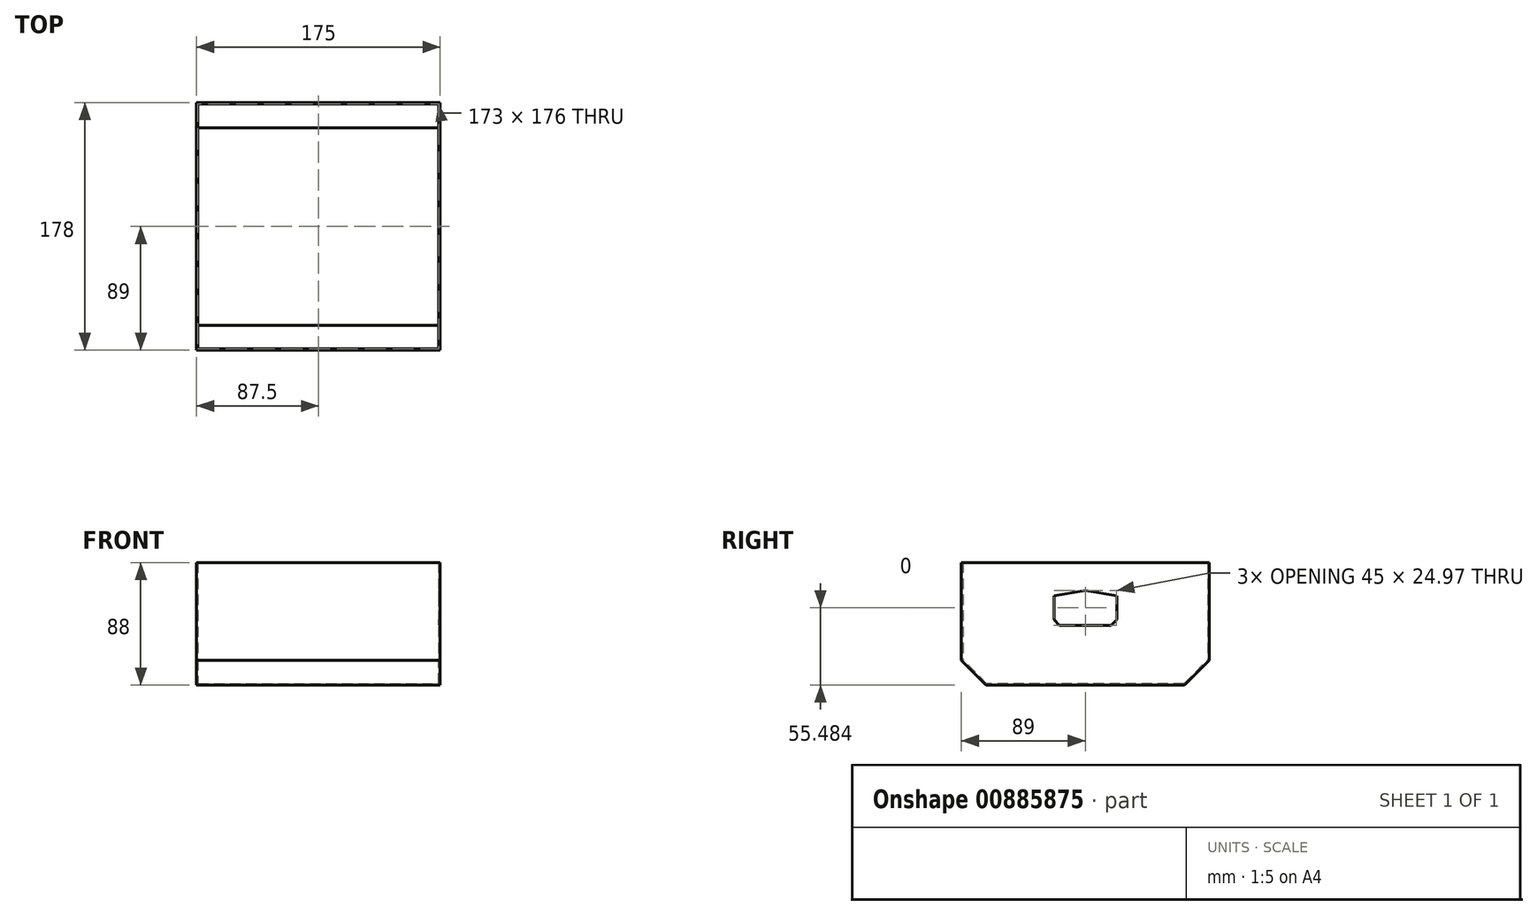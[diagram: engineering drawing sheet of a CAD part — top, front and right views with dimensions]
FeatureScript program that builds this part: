
annotation { "Feature Type Name" : "Feature", "Feature Type Description" : "" }
export const myFeature = defineFeature(function(context is Context, id is Id, definition is map)
    precondition{}
    {
        {
            var Q0;
            Q0=qCreatedBy(makeId("Top.planeOp"),FACE);
            var sketch = newSketch(context, id + "F0", { "sketchPlane" : qUnion([Q0])});
            skLineSegment(sketch, "E0.bottom", {"start": v(0, 0) * mm, "end": v(175, 0) * mm});
            skLineSegment(sketch, "E0.top", {"start": v(0, -178) * mm, "end": v(175, -178) * mm});
            skLineSegment(sketch, "E0.left", {"start": v(0, 0) * mm, "end": v(0, -178) * mm});
            skLineSegment(sketch, "E0.right", {"start": v(175, 0) * mm, "end": v(175, -178) * mm});
            skSolve(sketch);
        }
        {
            var Q0;
            Q0 = qSketchRegion(id + "F0", true);
            extrude(context, id + "F1", {"entities" : qUnion([Q0]), "depth" : 88 * mm, "offsetDistance" : 25 * mm});
        }
        {
            var Q0;
            Q0=makeQuery(id+"F1.opExtrude","CAP_EDGE",EDGE,{"disambiguationData":[OSD([sQuery(id+"F0.wireOp",EDGE,"E0.top")])],"isStart":true});
            var Q1;
            Q1=makeQuery(id+"F1.opExtrude","CAP_EDGE",EDGE,{"disambiguationData":[OSD([sQuery(id+"F0.wireOp",EDGE,"E0.bottom")])],"isStart":true});
            chamfer(context, id + "F2", {"entities" : qUnion([Q0, Q1]), "width" : 17.68 * mm, "tangentPropagation" : true});
        }
        {
            var Q0;
            Q0=makeQuery(id+"F1.opExtrude","CAP_FACE",FACE,{"disambiguationData":[OSD([sQuery(id+"F0.wireOp",EDGE,"E0.bottom"),sQuery(id+"F0.wireOp",EDGE,"E0.top"),sQuery(id+"F0.wireOp",EDGE,"E0.left"),sQuery(id+"F0.wireOp",EDGE,"E0.right")])],"isStart":false});
            shell(context, id + "F3", {"entities" : qUnion([Q0]), "thickness" : 1 * mm});
        }
        {
            var Q0;
            Q0=makeQuery(id+"F1.opExtrude","SWEPT_FACE",FACE,{"disambiguationData":[OSD([sQuery(id+"F0.wireOp",EDGE,"E0.right")])]});
            var sketch = newSketch(context, id + "F4", { "sketchPlane" : qUnion([Q0])});
            skLineSegment(sketch, "E1.bottom", {"start": v(-111.5, 68) * mm, "end": v(-66.5, 68) * mm});
            skLineSegment(sketch, "E1.top", {"start": v(-111.5, 43) * mm, "end": v(-66.5, 43) * mm});
            skLineSegment(sketch, "E1.left", {"start": v(-111.5, 68) * mm, "end": v(-111.5, 43) * mm});
            skLineSegment(sketch, "E1.right", {"start": v(-66.5, 68) * mm, "end": v(-66.5, 43) * mm});
            skSolve(sketch);
        }
        {
            var Q0;
            Q0 = qSketchRegion(id + "F4", true);
            extrude(context, id + "F5", {"entities" : qUnion([Q0]), "operationType" : NewBodyOperationType.REMOVE, "oppositeDirection" : true, "depth" : 2 * mm, "offsetDistance" : 25 * mm});
        }
        {
            var Q0;
            Q0=makeQuery(id+"F5.boolean.opBoolean","COPY",EDGE,{"derivedFrom":makeQuery(id+"F5.opExtrude","SWEPT_EDGE",EDGE,{"disambiguationData":[OSD([sQuery(id+"F4.wireOp",EDGE,"E1.bottom"),sQuery(id+"F4.wireOp",EDGE,"E1.left")])]})});
            var Q1;
            Q1=makeQuery(id+"F5.boolean.opBoolean","COPY",EDGE,{"derivedFrom":makeQuery(id+"F5.opExtrude","SWEPT_EDGE",EDGE,{"disambiguationData":[OSD([sQuery(id+"F4.wireOp",EDGE,"E1.bottom"),sQuery(id+"F4.wireOp",EDGE,"E1.right")])]})});
            chamfer(context, id + "F6", {"entities" : qUnion([Q0, Q1]), "chamferType" : ChamferType.OFFSET_ANGLE, "width" : 4 * mm, "oppositeDirection" : false, "angle" : 80 * degree, "tangentPropagation" : true});
        }
        {
            var Q0;
            Q0=makeQuery(id+"F5.boolean.opBoolean","COPY",EDGE,{"derivedFrom":makeQuery(id+"F5.opExtrude","SWEPT_EDGE",EDGE,{"disambiguationData":[OSD([sQuery(id+"F4.wireOp",EDGE,"E1.top"),sQuery(id+"F4.wireOp",EDGE,"E1.left")])]})});
            var Q1;
            Q1=makeQuery(id+"F5.boolean.opBoolean","COPY",EDGE,{"derivedFrom":makeQuery(id+"F5.opExtrude","SWEPT_EDGE",EDGE,{"disambiguationData":[OSD([sQuery(id+"F4.wireOp",EDGE,"E1.top"),sQuery(id+"F4.wireOp",EDGE,"E1.right")])]})});
            chamfer(context, id + "F7", {"entities" : qUnion([Q0, Q1]), "width" : 4 * mm, "tangentPropagation" : true});
        }
    });
